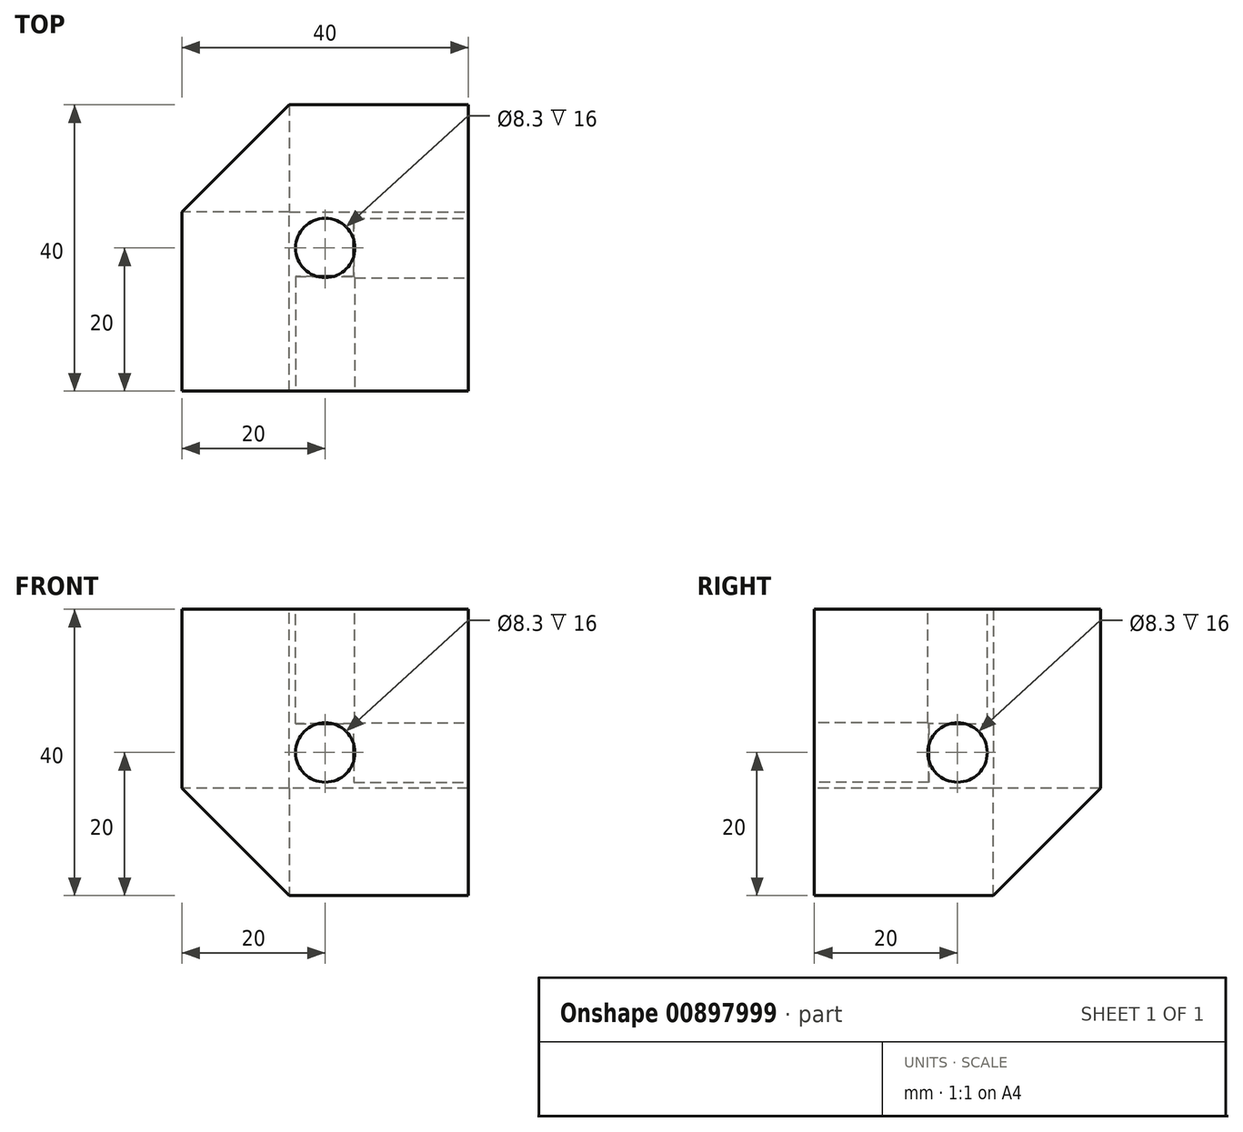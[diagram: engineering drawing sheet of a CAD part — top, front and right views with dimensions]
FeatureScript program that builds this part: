
annotation { "Feature Type Name" : "Feature", "Feature Type Description" : "" }
export const myFeature = defineFeature(function(context is Context, id is Id, definition is map)
    precondition{}
    {
        {
            var Q0;
            Q0=qCreatedBy(makeId("Top.planeOp"),FACE);
            var sketch = newSketch(context, id + "F0", { "sketchPlane" : qUnion([Q0])});
            skLineSegment(sketch, "E0.bottom", {"start": v(0, 0) * mm, "end": v(40, 0) * mm});
            skLineSegment(sketch, "E0.top", {"start": v(0, 40) * mm, "end": v(40, 40) * mm});
            skLineSegment(sketch, "E0.left", {"start": v(0, 0) * mm, "end": v(0, 40) * mm});
            skLineSegment(sketch, "E0.right", {"start": v(40, 0) * mm, "end": v(40, 40) * mm});
            skSolve(sketch);
        }
        {
            var Q0;
            Q0 = qSketchRegion(id + "F0", true);
            extrude(context, id + "F1", {"entities" : qUnion([Q0]), "depth" : 40 * mm, "offsetDistance" : 25 * mm});
        }
        {
            var Q0;
            Q0=makeQuery(id+"F1.opExtrude","SWEPT_FACE",FACE,{"disambiguationData":[OSD([sQuery(id+"F0.wireOp",EDGE,"E0.bottom")])]});
            var sketch = newSketch(context, id + "F2", { "sketchPlane" : qUnion([Q0])});
            skLineSegment(sketch, "E1", {"start": v(0, 40) * mm, "end": v(40, 0) * mm});
            skCircle(sketch, "E2", {"center": v(20, 20) * mm, "radius": 4.15 * mm});
            skSolve(sketch);
        }
        {
            var Q0;
            Q0 = qSketchRegion(id + "F2", true);
            extrude(context, id + "F3", {"entities" : qUnion([Q0]), "operationType" : NewBodyOperationType.REMOVE, "oppositeDirection" : true, "depth" : 16 * mm, "offsetDistance" : 25 * mm});
        }
        {
            var Q0;
            Q0=makeQuery(id+"F1.opExtrude","SWEPT_FACE",FACE,{"disambiguationData":[OSD([sQuery(id+"F0.wireOp",EDGE,"E0.right")])]});
            var sketch = newSketch(context, id + "F4", { "sketchPlane" : qUnion([Q0])});
            skLineSegment(sketch, "E3", {"start": v(0, 40) * mm, "end": v(40, 0) * mm});
            skCircle(sketch, "E4", {"center": v(20, 20) * mm, "radius": 4.15 * mm});
            skSolve(sketch);
        }
        {
            var Q0;
            {var subQ0=sQuery(id+"F4.wireOp",EDGE,"E4");var subQ1=sQuery(id+"F4.wireOp",EDGE,"E3");var subQ2=makeQuery(id+"F4.imprint","INTERSECT",VERTEX,{"disambiguationData":[OD(0.0)],"derivedFrom":[subQ1,subQ0]});Q0=makeQuery(id+"F4.imprint","IMPRINT",FACE,{"disambiguationData":[TD([[makeQuery(id+"F4.imprint","IMPRINT",EDGE,{"disambiguationData":[TD([[subQ2,-1.0]])],"derivedFrom":subQ1}),1.0]])]});}
            var Q1;
            {var subQ0=sQuery(id+"F4.wireOp",EDGE,"E4");var subQ1=sQuery(id+"F4.wireOp",EDGE,"E3");var subQ2=makeQuery(id+"F4.imprint","INTERSECT",VERTEX,{"disambiguationData":[OD(0.0)],"derivedFrom":[subQ1,subQ0]});Q1=makeQuery(id+"F4.imprint","IMPRINT",FACE,{"disambiguationData":[TD([[makeQuery(id+"F4.imprint","IMPRINT",EDGE,{"disambiguationData":[TD([[subQ2,-1.0]])],"derivedFrom":subQ1}),-1.0]])]});}
            extrude(context, id + "F5", {"entities" : qUnion([Q0, Q1]), "operationType" : NewBodyOperationType.REMOVE, "oppositeDirection" : true, "depth" : 16 * mm, "offsetDistance" : 25 * mm});
        }
        {
            var Q0;
            Q0=makeQuery(id+"F1.opExtrude","CAP_FACE",FACE,{"disambiguationData":[OSD([sQuery(id+"F0.wireOp",EDGE,"E0.bottom"),sQuery(id+"F0.wireOp",EDGE,"E0.top"),sQuery(id+"F0.wireOp",EDGE,"E0.left"),sQuery(id+"F0.wireOp",EDGE,"E0.right")])],"isStart":false});
            var sketch = newSketch(context, id + "F6", { "sketchPlane" : qUnion([Q0])});
            skLineSegment(sketch, "E5", {"start": v(0, 40) * mm, "end": v(40, 0) * mm});
            skCircle(sketch, "E6", {"center": v(20, 20) * mm, "radius": 4.15 * mm});
            skSolve(sketch);
        }
        {
            var Q0;
            {var subQ0=sQuery(id+"F6.wireOp",EDGE,"E6");var subQ1=sQuery(id+"F6.wireOp",EDGE,"E5");var subQ2=makeQuery(id+"F6.imprint","INTERSECT",VERTEX,{"disambiguationData":[OD(0.0)],"derivedFrom":[subQ1,subQ0]});Q0=makeQuery(id+"F6.imprint","IMPRINT",FACE,{"disambiguationData":[TD([[makeQuery(id+"F6.imprint","IMPRINT",EDGE,{"disambiguationData":[TD([[subQ2,-1.0]])],"derivedFrom":subQ1}),1.0]])]});}
            var Q1;
            {var subQ0=sQuery(id+"F6.wireOp",EDGE,"E6");var subQ1=sQuery(id+"F6.wireOp",EDGE,"E5");var subQ2=makeQuery(id+"F6.imprint","INTERSECT",VERTEX,{"disambiguationData":[OD(0.0)],"derivedFrom":[subQ1,subQ0]});Q1=makeQuery(id+"F6.imprint","IMPRINT",FACE,{"disambiguationData":[TD([[makeQuery(id+"F6.imprint","IMPRINT",EDGE,{"disambiguationData":[TD([[subQ2,-1.0]])],"derivedFrom":subQ1}),-1.0]])]});}
            extrude(context, id + "F7", {"entities" : qUnion([Q0, Q1]), "operationType" : NewBodyOperationType.REMOVE, "oppositeDirection" : true, "depth" : 16 * mm, "offsetDistance" : 25 * mm});
        }
        {
            var Q0;
            Q0=makeQuery(id+"F1.opExtrude","CAP_EDGE",EDGE,{"disambiguationData":[OSD([sQuery(id+"F0.wireOp",EDGE,"E0.top")])],"isStart":true});
            var Q1;
            Q1=makeQuery(id+"F1.opExtrude","CAP_EDGE",EDGE,{"disambiguationData":[OSD([sQuery(id+"F0.wireOp",EDGE,"E0.left")])],"isStart":true});
            var Q2;
            Q2=makeQuery(id+"F1.opExtrude","SWEPT_EDGE",EDGE,{"disambiguationData":[OSD([sQuery(id+"F0.wireOp",EDGE,"E0.top"),sQuery(id+"F0.wireOp",EDGE,"E0.left")])]});
            chamfer(context, id + "F8", {"entities" : qUnion([Q0, Q1, Q2]), "width" : 15 * mm, "tangentPropagation" : true});
        }
    });
